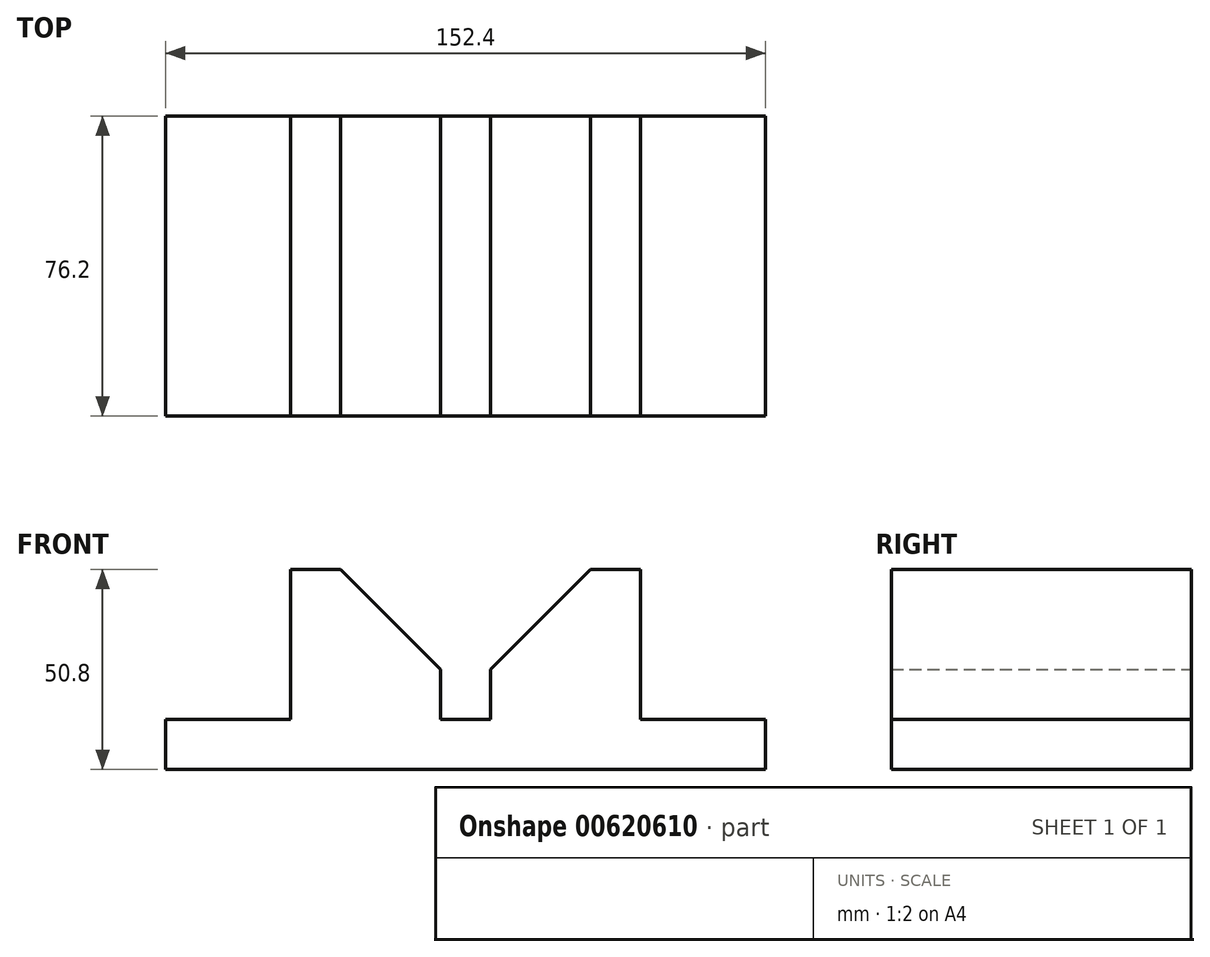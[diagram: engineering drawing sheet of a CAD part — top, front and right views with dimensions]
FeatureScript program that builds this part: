
annotation { "Feature Type Name" : "Feature", "Feature Type Description" : "" }
export const myFeature = defineFeature(function(context is Context, id is Id, definition is map)
    precondition{}
    {
        {
            var Q0;
            Q0=qCreatedBy(makeId("Front.planeOp"),FACE);
            var sketch = newSketch(context, id + "F0", { "sketchPlane" : qUnion([Q0])});
            skLineSegment(sketch, "E0", {"start": v(0, 0) * mm, "end": v(152.4, 0) * mm});
            skLineSegment(sketch, "E1", {"start": v(152.4, 0) * mm, "end": v(152.4, 12.7) * mm});
            skLineSegment(sketch, "E2", {"start": v(152.4, 12.7) * mm, "end": v(120.65, 12.7) * mm});
            skLineSegment(sketch, "E3", {"start": v(120.65, 12.7) * mm, "end": v(120.65, 50.8) * mm});
            skLineSegment(sketch, "E4", {"start": v(120.65, 50.8) * mm, "end": v(107.95, 50.8) * mm});
            skLineSegment(sketch, "E5", {"start": v(0, 0) * mm, "end": v(0, 12.7) * mm});
            skLineSegment(sketch, "E6", {"start": v(0, 12.7) * mm, "end": v(31.75, 12.7) * mm});
            skLineSegment(sketch, "E7", {"start": v(31.75, 12.7) * mm, "end": v(31.75, 50.8) * mm});
            skLineSegment(sketch, "E8", {"start": v(31.75, 50.8) * mm, "end": v(44.45, 50.8) * mm});
            skLineSegment(sketch, "E9", {"start": v(69.85, 12.7) * mm, "end": v(69.85, 25.4) * mm});
            skLineSegment(sketch, "E10", {"start": v(69.85, 12.7) * mm, "end": v(82.55, 12.7) * mm});
            skLineSegment(sketch, "E11", {"start": v(82.55, 12.7) * mm, "end": v(82.55, 25.4) * mm});
            skLineSegment(sketch, "E12", {"start": v(82.55, 25.4) * mm, "end": v(107.95, 50.8) * mm});
            skLineSegment(sketch, "E13", {"start": v(69.85, 25.4) * mm, "end": v(44.45, 50.8) * mm});
            skSolve(sketch);
        }
        {
            var Q0;
            Q0=makeQuery(id+"F0.imprint","IMPRINT",FACE,{"disambiguationData":[TD([[makeQuery(id+"F0.imprint","IMPRINT",EDGE,{"derivedFrom":sQuery(id+"F0.wireOp",EDGE,"E0")}),1.0]])]});
            extrude(context, id + "F1", {"entities" : qUnion([Q0]), "depth" : 76.2 * mm, "offsetDistance" : 25.4 * mm});
        }
    });
